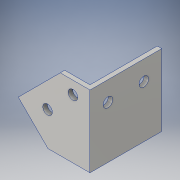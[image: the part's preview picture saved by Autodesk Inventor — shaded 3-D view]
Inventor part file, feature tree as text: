
AUTODESK INVENTOR PART (.ipt)
format: ipt  version: 2016 (Build 200138000, 138)  size: 141,312 bytes
history: native  units: in
note: dims shown in document units (in); Inventor stores cm internally (conversion verified against a paired STEP export)
features: extrude x4, sketch x4
ambient origin geometry x8: Origin, YZ Plane, XZ Plane, XY Plane, X Axis, Y Axis, Z Axis, Center Point
bodies: Solid1 (feature_tree)
feature tree (8):
  extrude  "Extrusion1"  Depth=2.0in
  extrude  "Extrusion2"  TaperAngle=135.0deg  [1 undecoded]
  extrude  "Extrusion3"  Depth=0.125in
  extrude  "Extrusion4"  Depth=0.125in
  sketch  "Sketch1"  dims[d0=2.0in d2=2.0in]
  sketch  "Sketch2"  dims[d3=2.0in d4=135.0deg]
  sketch  "Sketch3"  dims[d5=0.125in d6=0.0in d7=0.125in]
  sketch  "Sketch4"  dims[d8=2.0in d9=0.0in d10=0.2656in d11=0.2656in d12=0.546in d13=0.546in d14=0.5in d15=1.0in d16=0.125in d17=0.0in d18=0.656in d19=0.5in d20=0.5in d21=0.2656in d22=1.0in d23=0.125in d24=0.0in d25=0.4755in d26=1.1826in d27=0.3542in d28=1.0613in d29=0.9387in]
note: 1 required parameter value undecoded (feature->parameter linkage not recoverable at this tier; creation-order binding heuristic only, values carry confidence <= 0.55)
